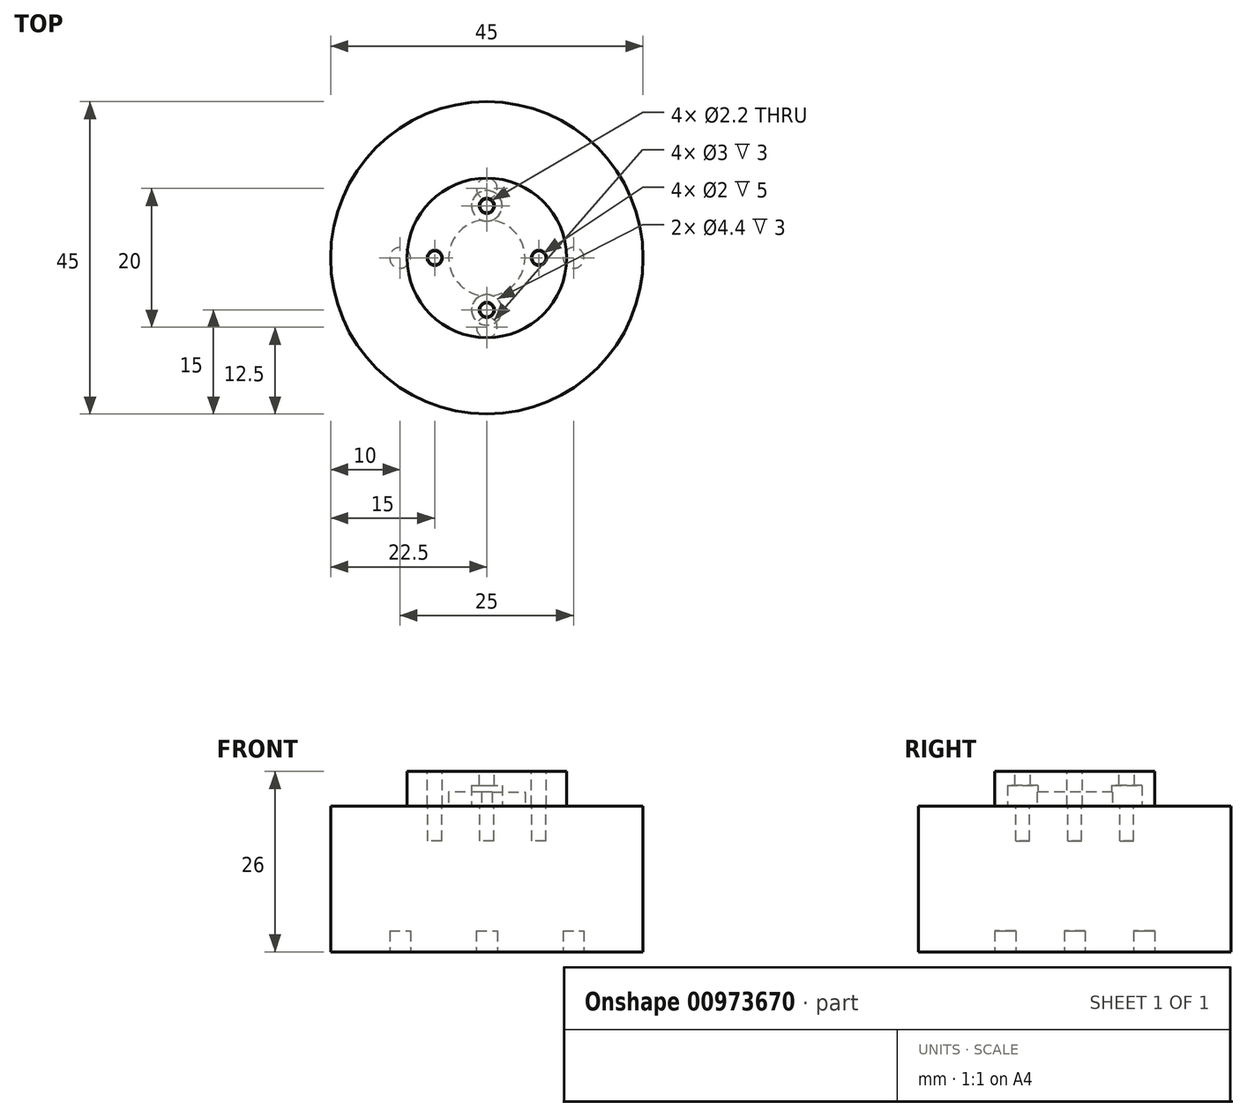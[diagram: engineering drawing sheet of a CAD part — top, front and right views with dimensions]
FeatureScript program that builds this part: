
annotation { "Feature Type Name" : "Feature", "Feature Type Description" : "" }
export const myFeature = defineFeature(function(context is Context, id is Id, definition is map)
    precondition{}
    {
        {
            var Q0;
            Q0=qCreatedBy(makeId("Top.planeOp"),FACE);
            var sketch = newSketch(context, id + "F0", { "sketchPlane" : qUnion([Q0])});
            skCircle(sketch, "E0", {"center": v(0, 0) * mm, "radius": 22.5 * mm});
            skSolve(sketch);
        }
        {
            var Q0;
            Q0=makeQuery(id+"F0.imprint","IMPRINT",FACE,{"disambiguationData":[TD([[makeQuery(id+"F0.imprint","IMPRINT",EDGE,{"derivedFrom":sQuery(id+"F0.wireOp",EDGE,"E0")}),1.0]])]});
            extrude(context, id + "F1", {"entities" : qUnion([Q0]), "depth" : 21 * mm, "offsetDistance" : 25 * mm});
        }
        {
            var Q0;
            Q0=makeQuery(id+"F1.opExtrude","CAP_FACE",FACE,{"disambiguationData":[OSD([sQuery(id+"F0.wireOp",EDGE,"E0")])],"isStart":true});
            var sketch = newSketch(context, id + "F2", { "sketchPlane" : qUnion([Q0])});
            skCircle(sketch, "E1", {"center": v(0, 0) * mm, "radius": 12.5 * mm, "construction": true});
            skCircle(sketch, "E2", {"center": v(0, 0) * mm, "radius": 10 * mm, "construction": true});
            skCircle(sketch, "E3", {"center": v(0, 10) * mm, "radius": 1.5 * mm});
            skCircle(sketch, "E4", {"center": v(0, -10) * mm, "radius": 1.5 * mm});
            skCircle(sketch, "E5", {"center": v(12.5, 0) * mm, "radius": 1.5 * mm});
            skCircle(sketch, "E6", {"center": v(-12.5, 0) * mm, "radius": 1.5 * mm});
            skSolve(sketch);
        }
        {
            var Q0;
            Q0 = qSketchRegion(id + "F2", true);
            extrude(context, id + "F3", {"entities" : qUnion([Q0]), "operationType" : NewBodyOperationType.REMOVE, "oppositeDirection" : true, "depth" : 3 * mm, "offsetDistance" : 25 * mm});
        }
        {
            var Q0;
            Q0=makeQuery(id+"F1.opExtrude","CAP_FACE",FACE,{"disambiguationData":[OSD([sQuery(id+"F0.wireOp",EDGE,"E0")])],"isStart":false});
            var sketch = newSketch(context, id + "F4", { "sketchPlane" : qUnion([Q0])});
            skCircle(sketch, "E7", {"center": v(0, 0) * mm, "radius": 5 * mm});
            skSolve(sketch);
        }
        {
            var Q0;
            Q0 = qSketchRegion(id + "F4", true);
            extrude(context, id + "F5", {"entities" : qUnion([Q0]), "operationType" : NewBodyOperationType.ADD, "depth" : 1.2 * mm, "offsetDistance" : 25 * mm});
        }
        {
            var Q0;
            Q0=makeQuery(id+"F1.opExtrude","CAP_FACE",FACE,{"disambiguationData":[OSD([sQuery(id+"F0.wireOp",EDGE,"E0")])],"isStart":false});
            var sketch = newSketch(context, id + "F6", { "sketchPlane" : qUnion([Q0])});
            skCircle(sketch, "E8", {"center": v(0, 7.5) * mm, "radius": 1 * mm});
            skCircle(sketch, "E9", {"center": v(0, -7.5) * mm, "radius": 1 * mm});
            skCircle(sketch, "E10", {"center": v(7.5, 0) * mm, "radius": 1 * mm});
            skCircle(sketch, "E11", {"center": v(-7.5, 0) * mm, "radius": 1 * mm});
            skLineSegment(sketch, "E12", {"start": v(-7.5, 0) * mm, "end": v(7.5, 0) * mm, "construction": true});
            skLineSegment(sketch, "E13", {"start": v(0, 7.5) * mm, "end": v(0, -7.5) * mm, "construction": true});
            skPoint(sketch, "E14", {"position": v(0, 0) * mm});
            skSolve(sketch);
        }
        {
            var Q0;
            Q0 = qSketchRegion(id + "F6", true);
            extrude(context, id + "F7", {"entities" : qUnion([Q0]), "operationType" : NewBodyOperationType.REMOVE, "oppositeDirection" : true, "depth" : 5 * mm, "offsetDistance" : 25 * mm});
        }
        {
            var Q0;
            Q0=makeQuery(id+"F1.opExtrude","CAP_FACE",FACE,{"disambiguationData":[OSD([sQuery(id+"F0.wireOp",EDGE,"E0")])],"isStart":false});
            var sketch = newSketch(context, id + "F8", { "sketchPlane" : qUnion([Q0])});
            skCircle(sketch, "E15", {"center": v(0, 0) * mm, "radius": 11.5 * mm});
            skSolve(sketch);
        }
        {
            var Q0;
            Q0 = qSketchRegion(id + "F8", true);
            extrude(context, id + "F9", {"entities" : qUnion([Q0]), "depth" : 5 * mm, "offsetDistance" : 25 * mm});
        }
        {
            var Q0;
            Q0=makeQuery(id+"F9.opExtrude","CAP_FACE",FACE,{"disambiguationData":[OSD([sQuery(id+"F8.wireOp",EDGE,"E15")])],"isStart":true});
            var sketch = newSketch(context, id + "F10", { "sketchPlane" : qUnion([Q0])});
            skCircle(sketch, "E16", {"center": v(0, 0) * mm, "radius": 5.5 * mm});
            skSolve(sketch);
        }
        {
            var Q0;
            Q0 = qSketchRegion(id + "F10", true);
            extrude(context, id + "F11", {"entities" : qUnion([Q0]), "operationType" : NewBodyOperationType.REMOVE, "oppositeDirection" : true, "depth" : 2 * mm, "offsetDistance" : 25 * mm});
        }
        {
            var Q0;
            Q0=makeQuery(id+"F9.opExtrude","CAP_FACE",FACE,{"disambiguationData":[OSD([sQuery(id+"F8.wireOp",EDGE,"E15")])],"isStart":false});
            var sketch = newSketch(context, id + "F12", { "sketchPlane" : qUnion([Q0])});
            skCircle(sketch, "E17.0", {"center": v(-7.5, 0) * mm, "radius": 1.1 * mm});
            skCircle(sketch, "E17.1", {"center": v(0, 7.5) * mm, "radius": 1.1 * mm});
            skCircle(sketch, "E17.2", {"center": v(7.5, 0) * mm, "radius": 1.1 * mm});
            skCircle(sketch, "E17.3", {"center": v(0, -7.5) * mm, "radius": 1.1 * mm});
            skSolve(sketch);
        }
        {
            var Q0;
            Q0 = qSketchRegion(id + "F12", true);
            extrude(context, id + "F13", {"entities" : qUnion([Q0]), "operationType" : NewBodyOperationType.REMOVE, "endBound" : BoundingType.UP_TO_NEXT, "oppositeDirection" : true, "depth" : 25 * mm, "offsetDistance" : 25 * mm});
        }
        {
            var Q0;
            Q0=makeQuery(id+"F9.opExtrude","CAP_FACE",FACE,{"disambiguationData":[OSD([sQuery(id+"F8.wireOp",EDGE,"E15")])],"isStart":true});
            var sketch = newSketch(context, id + "F14", { "sketchPlane" : qUnion([Q0])});
            skCircle(sketch, "E18", {"center": v(0, 7.5) * mm, "radius": 2.2 * mm});
            skCircle(sketch, "E19", {"center": v(0, -7.5) * mm, "radius": 2.2 * mm});
            skSolve(sketch);
        }
        {
            var Q0;
            Q0 = qSketchRegion(id + "F14", true);
            extrude(context, id + "F15", {"entities" : qUnion([Q0]), "operationType" : NewBodyOperationType.REMOVE, "oppositeDirection" : true, "depth" : 3 * mm, "offsetDistance" : 25 * mm});
        }
    });
